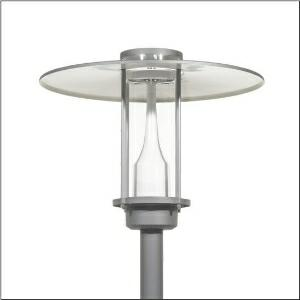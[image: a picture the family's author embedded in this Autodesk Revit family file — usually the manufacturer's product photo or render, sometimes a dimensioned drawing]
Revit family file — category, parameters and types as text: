
# Revit family: city-light_plus_iq___st1_2a_5xa5275ef14h_075f
name_source: partatom
category: Lighting Fixtures
units: mm (PartAtom-declared; Revit-internal decimal feet)

## family parameters
Cut with Voids When Loaded = No
Host = Face
Light Source = No
Part Type = Normal
Room Calculation Point = No
Round Connector Dimension = Use Diameter
Shared = No

## types (1)
- --- (1 x LED, 1470 lm, 10.5 W, 3000K)
    Apparent Load = 11 VA
    CIE Flux Codes = 22 62 93 97 100
    Color Rendering = 70
    Color Temperature = 3000K
    Default Elevation = 1800 mm
    Description = City-Light Plus iQ, mast luminaire, Module 540 iQ-SR, primary light control with 3 zone facetted reflector, of plastic, silver coated, highly specular, structured, primary optical cover: cover, of PMMA, transparent, light distribution: ST1.2a, light emission: direct distribution, primary light characteristic: asymmetric, installation type: post-top, LED, High Power LED, rated luminous flux: 1.470lm, luminous efficacy: 140lm/W, light colour: 730, colour temperature: 3000K, control gear: iQ Street-Remote, control: Auto-Match, Temp-Guard, Lumen-Switch, Night-Set, Smart-Wire, Light-Fading, Desk-Remote (wireless, voltage-free reading and setting of iQ features in the workshop via application-optimized NFC function/RFID function), optimised constant luminous flux control (CLO 2.0), Street-Remote, pre-setting: logarithmic dimming characteristic, with terminal, 6-pole, max. 2.5mm², mains connection: 230..240V, AC, 50/60Hz, start of lifetime: 11W, end of service life: 11W, reduction: 5W, luminaire housing, upper part, of glass-fibre reinforced polyester, coated, Siteco® metallic grey (DB 702S), diameter: 750mm, height: 590mm, spigot size: d x l = 76 x 70mm (post-top) | with reducer (optional accessory) 60 x 70mm, mounting height: 3..5m, post-top mast mounting element, of diecast aluminium, coated, Siteco® metallic grey (DB 702S), Module 540 iQ-SR, traffic white (RAL 9016), equipment: standard, protection rating (complete): IP65, insulation class (complete): insulation class II (safety insulation), certification: CE, ENEC, VDE, packaging unit: 1 piece

Light Distribution: ST1.2a
    Height = 590 mm
    Lamp = 1 x LED
    Lamp Light Flux = 1470 lm
    Lamp Power = 10.5 W
    Lamp count = 1
    Length = 750 mm
    Luminous efficacy = 140 lm/W
    Manufacturer = Siteco
    ModVariant = No
    Model = 5XA5275EF14H
    Number of Poles = 1
    OnlyDefault = Yes
    Power Factor = 1
    Product Name = City-Light Plus iQ | ST1.2a
    Product group = mast luminaire | pylon top
    ProductGroupID = 6100
    Protection Class = Protection class II
    Protection Degree = IP 65
    RLX_Detail_Level = 1
    RLX_Emergency_Light_Flux = 0 lm
    RLX_Emergency_Type = 0
    RLX_Emergency_Type_DB = No
    RlxData = <blob elided: 91425 chars, md5=f73a9c0c>
    Socket = socket
    Standby Power = 0 W
    System Light Flux = 1470 lm
    System Power = 11 W
    Type Comments = factory setting: luminous flux: 100 % | dim-lin: 254 | 419 mA
    Type Image = l_1006456.jpg
    URL = http://relux.com
    VarID = @adj_160140
    Voltage = 0 V
    Weight = 0.00 kg
    Width = 0 mm  [stored 0 ft]

note: [stored X ft] marks values corroborated as IEEE doubles in the binary element streams (Revit-internal decimal feet)

## geometry (parser evidence)
native form markers: Blend x4, Sweep x12
no freeform markers — native parametric forms only
